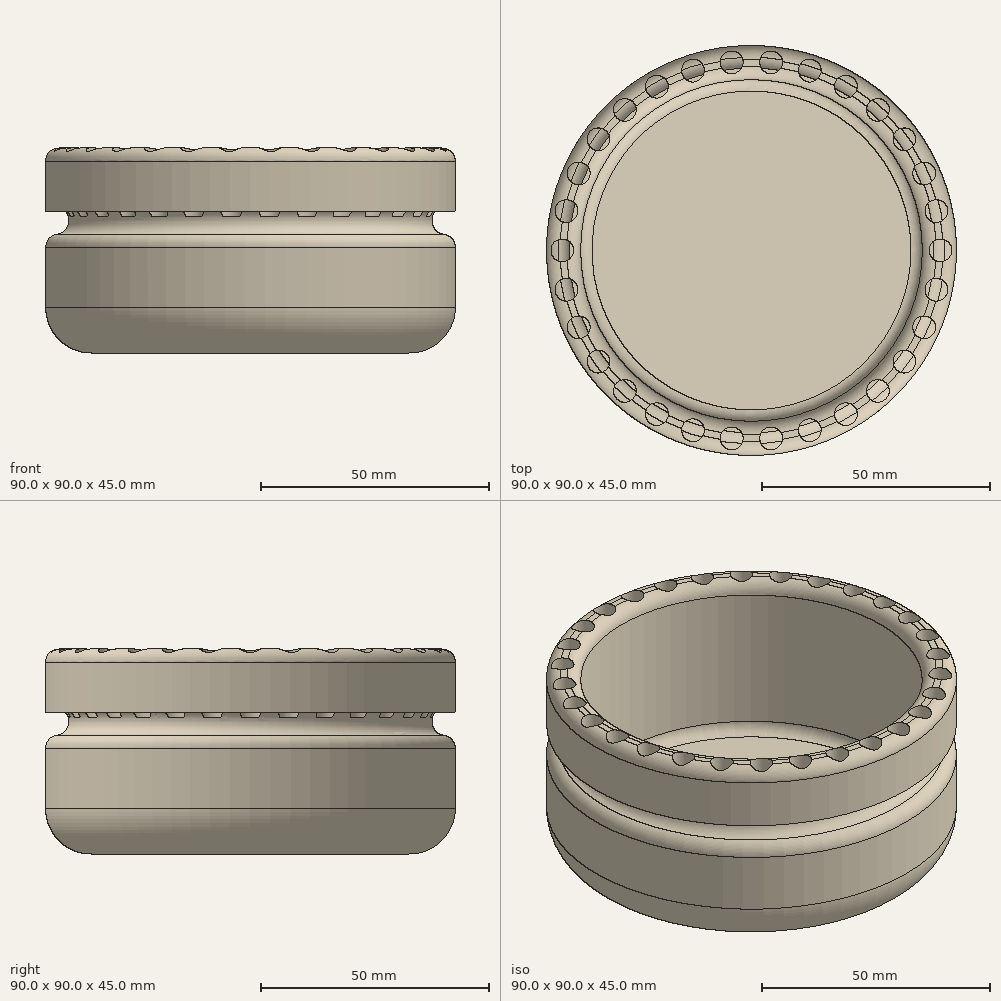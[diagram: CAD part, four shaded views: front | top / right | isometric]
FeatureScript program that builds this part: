
annotation { "Feature Type Name" : "Feature", "Feature Type Description" : "" }
export const myFeature = defineFeature(function(context is Context, id is Id, definition is map)
    precondition{}
    {
        {
            var Q0;
            Q0=qCreatedBy(makeId("Top.planeOp"),FACE);
            var sketch = newSketch(context, id + "F0", { "sketchPlane" : qUnion([Q0])});
            skCircle(sketch, "E0", {"center": v(0, 0) * mm, "radius": 45 * mm});
            skSolve(sketch);
        }
        {
            var Q0;
            Q0 = qSketchRegion(id + "F0", true);
            extrude(context, id + "F1", {"entities" : qUnion([Q0]), "depth" : 45 * mm});
        }
        {
            var Q0;
            Q0=makeQuery(id+"F1.opExtrude","CAP_FACE",FACE,{"disambiguationData":[OSD([sQuery(id+"F0.wireOp",EDGE,"E0")])],"isStart":true});
            fillet(context, id + "F2", {"entities" : qUnion([Q0]), "radius" : 10 * mm, "tangentPropagation" : true, "allowEdgeOverflow" : false});
        }
        {
            var Q0;
            Q0=makeQuery(id+"F1.opExtrude","CAP_FACE",FACE,{"disambiguationData":[OSD([sQuery(id+"F0.wireOp",EDGE,"E0")])],"isStart":false});
            shell(context, id + "F3", {"entities" : qUnion([Q0]), "thickness" : 7.5 * mm});
        }
        {
            var Q0;
            Q0=makeQuery(id+"F1.opExtrude","CAP_FACE",FACE,{"disambiguationData":[OSD([sQuery(id+"F0.wireOp",EDGE,"E0")])],"isStart":false});
            cPlane(context, id + "F4", {"entities" : qUnion([Q0]), "cplaneType" : CPlaneType.OFFSET, "offset" : 0 * mm, "width" : 150 * mm, "height" : 150 * mm});
        }
        {
            var Q0;
            Q0=qCreatedBy(id+"F4.planeOp",FACE);
            var sketch = newSketch(context, id + "F5", { "sketchPlane" : qUnion([Q0])});
            skCircle(sketch, "E1", {"center": v(-41.5, 0) * mm, "radius": 2.5 * mm});
            skCircle(sketch, "E2.1.0", {"center": v(-40.6, -8.63) * mm, "radius": 2.5 * mm});
            skCircle(sketch, "E2.2.0", {"center": v(-37.92, -16.88) * mm, "radius": 2.5 * mm});
            skCircle(sketch, "E2.3.0", {"center": v(-33.58, -24.4) * mm, "radius": 2.5 * mm});
            skCircle(sketch, "E2.4.0", {"center": v(-27.77, -30.84) * mm, "radius": 2.5 * mm});
            skCircle(sketch, "E2.5.0", {"center": v(-20.75, -35.94) * mm, "radius": 2.5 * mm});
            skCircle(sketch, "E2.6.0", {"center": v(-12.83, -39.47) * mm, "radius": 2.5 * mm});
            skCircle(sketch, "E2.7.0", {"center": v(-4.34, -41.28) * mm, "radius": 2.5 * mm});
            skCircle(sketch, "E2.8.0", {"center": v(4.34, -41.28) * mm, "radius": 2.5 * mm});
            skCircle(sketch, "E2.9.0", {"center": v(12.83, -39.47) * mm, "radius": 2.5 * mm});
            skCircle(sketch, "E2.10.0", {"center": v(20.75, -35.94) * mm, "radius": 2.5 * mm});
            skCircle(sketch, "E2.11.0", {"center": v(27.77, -30.84) * mm, "radius": 2.5 * mm});
            skCircle(sketch, "E2.12.0", {"center": v(33.58, -24.4) * mm, "radius": 2.5 * mm});
            skCircle(sketch, "E2.13.0", {"center": v(37.92, -16.88) * mm, "radius": 2.5 * mm});
            skCircle(sketch, "E2.14.0", {"center": v(40.6, -8.63) * mm, "radius": 2.5 * mm});
            skCircle(sketch, "E2.15.0", {"center": v(41.5, 0) * mm, "radius": 2.5 * mm});
            skCircle(sketch, "E2.16.0", {"center": v(40.6, 8.63) * mm, "radius": 2.5 * mm});
            skCircle(sketch, "E2.17.0", {"center": v(37.92, 16.88) * mm, "radius": 2.5 * mm});
            skCircle(sketch, "E2.18.0", {"center": v(33.58, 24.4) * mm, "radius": 2.5 * mm});
            skCircle(sketch, "E2.19.0", {"center": v(27.77, 30.84) * mm, "radius": 2.5 * mm});
            skCircle(sketch, "E2.20.0", {"center": v(20.75, 35.94) * mm, "radius": 2.5 * mm});
            skCircle(sketch, "E2.21.0", {"center": v(12.83, 39.47) * mm, "radius": 2.5 * mm});
            skCircle(sketch, "E2.22.0", {"center": v(4.34, 41.28) * mm, "radius": 2.5 * mm});
            skCircle(sketch, "E2.23.0", {"center": v(-4.34, 41.28) * mm, "radius": 2.5 * mm});
            skCircle(sketch, "E2.24.0", {"center": v(-12.83, 39.47) * mm, "radius": 2.5 * mm});
            skCircle(sketch, "E2.25.0", {"center": v(-20.75, 35.94) * mm, "radius": 2.5 * mm});
            skCircle(sketch, "E2.26.0", {"center": v(-27.77, 30.84) * mm, "radius": 2.5 * mm});
            skCircle(sketch, "E2.27.0", {"center": v(-33.58, 24.4) * mm, "radius": 2.5 * mm});
            skCircle(sketch, "E2.28.0", {"center": v(-37.92, 16.88) * mm, "radius": 2.5 * mm});
            skCircle(sketch, "E2.29.0", {"center": v(-40.6, 8.63) * mm, "radius": 2.5 * mm});
            skPoint(sketch, "E2.center", {"position": v(0, 0) * mm});
            skSolve(sketch);
        }
        {
            var Q0;
            Q0 = qSketchRegion(id + "F5", true);
            extrude(context, id + "F6", {"entities" : qUnion([Q0]), "operationType" : NewBodyOperationType.REMOVE, "oppositeDirection" : true, "depth" : 15 * mm});
        }
        {
            var Q0;
            Q0=qCreatedBy(makeId("Front.planeOp"),FACE);
            var sketch = newSketch(context, id + "F7", { "sketchPlane" : qUnion([Q0])});
            skCircle(sketch, "E3", {"center": v(-42.86, 29.03) * mm, "radius": 3 * mm});
            skLineSegment(sketch, "E4", {"start": v(0, 0) * mm, "end": v(0, 42.42) * mm});
            skSolve(sketch);
        }
        {
            var Q0;
            Q0 = qSketchRegion(id + "F7", true);
            var Q1;
            Q1=sQuery(id+"F7.wireOp",EDGE,"E4");
            revolve(context, id + "F8", {"operationType" : NewBodyOperationType.REMOVE, "entities" : qUnion([Q0]), "axis" : qUnion([Q1]), "revolveType" : RevolveType.FULL, "oppositeDirection" : true});
        }
        {
            var Q0;
            Q0=makeQuery(id+"F8.boolean.opBoolean","INTERSECT",EDGE,{"disambiguationData":[OD(1.0)],"derivedFrom":[makeQuery(id+"F1.opExtrude","SWEPT_FACE",FACE,{"disambiguationData":[OSD([sQuery(id+"F0.wireOp",EDGE,"E0")])]}),makeQuery(id+"F8.opRevolve","SWEPT_FACE",FACE,{"disambiguationData":[OSD([sQuery(id+"F7.wireOp",EDGE,"E3")])]})]});
            fillet(context, id + "F9", {"entities" : qUnion([Q0]), "radius" : 3 * mm, "tangentPropagation" : true, "allowEdgeOverflow" : false});
        }
        {
            var Q0;
            Q0=makeQuery(id+"F1.opExtrude","CAP_EDGE",EDGE,{"disambiguationData":[OSD([sQuery(id+"F0.wireOp",EDGE,"E0")])],"isStart":false});
            var Q1;
            {var subQ0=sQuery(id+"F0.wireOp",EDGE,"E0");Q1=makeQuery(id+"F3.opShell","OFFSET_EDGE",EDGE,{"disambiguationData":[OSD([subQ0]),TDD([makeQuery(id+"F1.opExtrude","CAP_EDGE",EDGE,{"disambiguationData":[OSD([subQ0])],"isStart":false})])]});}
            fillet(context, id + "F10", {"entities" : qUnion([Q0, Q1]), "radius" : 3 * mm, "tangentPropagation" : true, "allowEdgeOverflow" : false});
        }
    });
